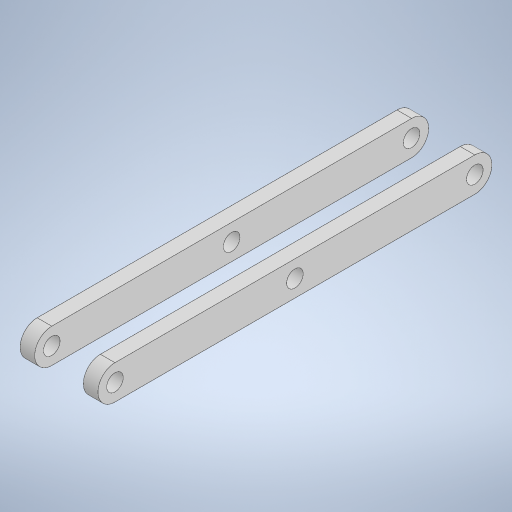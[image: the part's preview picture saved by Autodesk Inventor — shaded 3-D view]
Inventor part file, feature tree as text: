
AUTODESK INVENTOR PART (.ipt)
format: ipt  version: 2024.3 (Build 283343000, 343)  size: 255,488 bytes
history: native  units: mm
features: sketch x2, extrude x2, hole x1
ambient origin geometry x8: Origin, YZ Plane, XZ Plane, XY Plane, X Axis, Y Axis, Z Axis, Center Point
bodies: Body1 (feature_tree)
feature tree (5):
  sketch  "Sketch1"  dims[d14=7.0mm d15=81.0mm]
  extrude  "Extrusión3"  Depth=7.0mm
  extrude  "Extrusión4"  Depth=16.0mm TaperAngle=0.0deg
  hole  "Agujero1"  [1 undecoded]
  sketch  "Boceto2"  dims[d16=3.0mm d17=16.0mm d18=0.0mm d19=10.0mm d20=0.0mm d21=3.4mm d22=6.0mm d23=6.3mm d24=2.0mm d25=90.0deg d26=8.0mm d27=20.594885mm]
note: 1 required parameter value undecoded (feature->parameter linkage not recoverable at this tier; creation-order binding heuristic only, values carry confidence <= 0.55)
